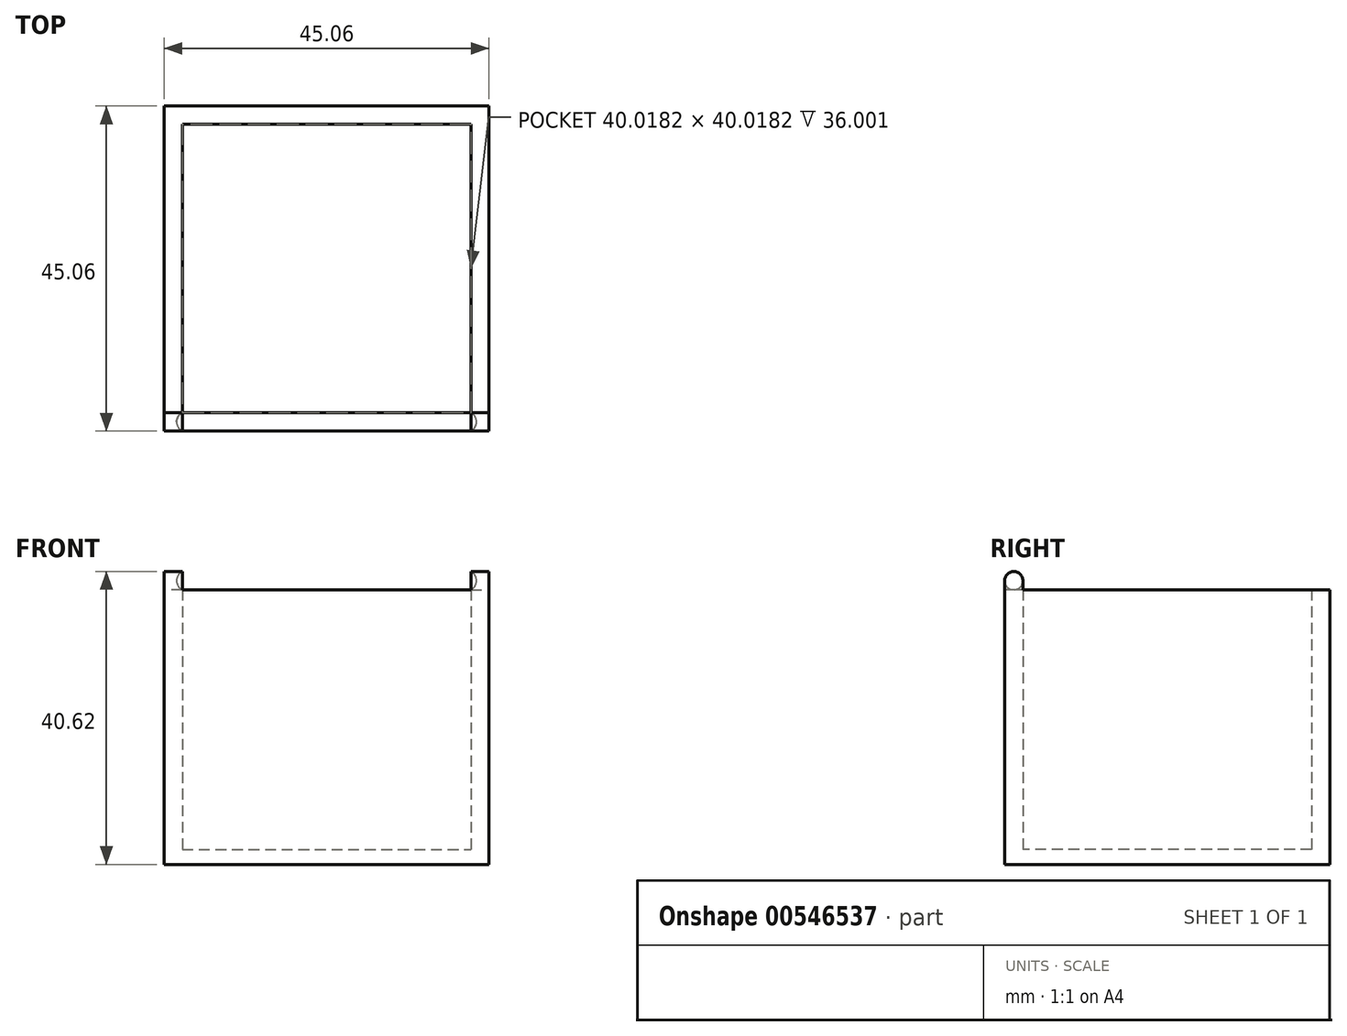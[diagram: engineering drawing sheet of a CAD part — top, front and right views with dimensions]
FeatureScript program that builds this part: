
annotation { "Feature Type Name" : "Feature", "Feature Type Description" : "" }
export const myFeature = defineFeature(function(context is Context, id is Id, definition is map)
    precondition{}
    {
        {
            var Q0;
            Q0=qCreatedBy(makeId("Top.planeOp"),FACE);
            var sketch = newSketch(context, id + "F0", { "sketchPlane" : qUnion([Q0])});
            skCircle(sketch, "E0.cCircle", {"center": v(0, 0) * mm, "radius": 22.53 * mm, "construction": true});
            skLineSegment(sketch, "E0.0", {"start": v(-22.53, -22.53) * mm, "end": v(-22.53, 22.53) * mm});
            skLineSegment(sketch, "E0.1", {"start": v(-22.53, 22.53) * mm, "end": v(22.53, 22.53) * mm});
            skLineSegment(sketch, "E0.2", {"start": v(22.53, 22.53) * mm, "end": v(22.53, -22.53) * mm});
            skLineSegment(sketch, "E0.3", {"start": v(22.53, -22.53) * mm, "end": v(-22.53, -22.53) * mm});
            skPoint(sketch, "E0.0.midPoint", {"position": v(-22.53, 0) * mm});
            skCircle(sketch, "E1.cCircle", {"center": v(0, 0) * mm, "radius": 20 * mm, "construction": true});
            skLineSegment(sketch, "E1.0", {"start": v(-20, -20) * mm, "end": v(-20, 20) * mm});
            skLineSegment(sketch, "E1.1", {"start": v(-20, 20) * mm, "end": v(20, 20) * mm});
            skLineSegment(sketch, "E1.2", {"start": v(20, 20) * mm, "end": v(20, -20) * mm});
            skLineSegment(sketch, "E1.3", {"start": v(20, -20) * mm, "end": v(-20, -20) * mm});
            skPoint(sketch, "E1.0.midPoint", {"position": v(-20, 0) * mm});
            skSolve(sketch);
        }
        {
            var Q0;
            Q0=makeQuery(id+"F0.imprint","IMPRINT",FACE,{"disambiguationData":[TD([[makeQuery(id+"F0.imprint","IMPRINT",EDGE,{"derivedFrom":sQuery(id+"F0.wireOp",EDGE,"E0.0")}),-1.0]])]});
            extrude(context, id + "F1", {"entities" : qUnion([Q0]), "depth" : 38.1 * mm, "offsetDistance" : 25.4 * mm});
        }
        {
            var Q0;
            Q0=makeQuery(id+"F1.opExtrude","CAP_FACE",FACE,{"disambiguationData":[OSD([sQuery(id+"F0.wireOp",EDGE,"E0.0"),sQuery(id+"F0.wireOp",EDGE,"E0.1"),sQuery(id+"F0.wireOp",EDGE,"E0.2"),sQuery(id+"F0.wireOp",EDGE,"E0.3"),sQuery(id+"F0.wireOp",EDGE,"E1.0"),sQuery(id+"F0.wireOp",EDGE,"E1.1"),sQuery(id+"F0.wireOp",EDGE,"E1.2"),sQuery(id+"F0.wireOp",EDGE,"E1.3")])],"isStart":false});
            var sketch = newSketch(context, id + "F2", { "sketchPlane" : qUnion([Q0])});
            skLineSegment(sketch, "E2.bottom", {"start": v(-20, -20) * mm, "end": v(-22.53, -20) * mm});
            skLineSegment(sketch, "E2.top", {"start": v(-20, -22.53) * mm, "end": v(-22.53, -22.53) * mm});
            skLineSegment(sketch, "E2.right", {"start": v(-22.53, -20) * mm, "end": v(-22.53, -22.53) * mm});
            skLineSegment(sketch, "E3.MirrorCS", {"start": v(20, -20) * mm, "end": v(22.53, -20) * mm});
            skLineSegment(sketch, "E4.MirrorCS", {"start": v(22.53, -20) * mm, "end": v(22.53, -22.53) * mm});
            skLineSegment(sketch, "E5.MirrorCS", {"start": v(20, -22.53) * mm, "end": v(22.53, -22.53) * mm});
            skLineSegment(sketch, "E6", {"start": v(-20, -20) * mm, "end": v(-20, -22.53) * mm});
            skLineSegment(sketch, "E7", {"start": v(20, -20) * mm, "end": v(20, -22.53) * mm});
            skSolve(sketch);
        }
        {
            var Q0;
            Q0 = qSketchRegion(id + "F2", true);
            extrude(context, id + "F3", {"entities" : qUnion([Q0]), "operationType" : NewBodyOperationType.ADD, "depth" : 1.26 * mm, "offsetDistance" : 25.4 * mm});
        }
        {
            var Q0;
            Q0=makeQuery(id+"F3.opExtrude","CAP_FACE",FACE,{"disambiguationData":[OSD([sQuery(id+"F2.wireOp",EDGE,"E2.bottom"),sQuery(id+"F2.wireOp",EDGE,"E2.top"),sQuery(id+"F2.wireOp",EDGE,"E2.right"),sQuery(id+"F2.wireOp",EDGE,"E6")])],"isStart":false});
            var sketch = newSketch(context, id + "F4", { "sketchPlane" : qUnion([Q0])});
            skPoint(sketch, "E8", {"position": v(-20, -21.27) * mm});
            skArc(sketch, "E9", {"start": v(-20, -20) * mm, "mid": v(-20.79, -21.27) * mm, "end": v(-20, -22.53) * mm});
            skLineSegment(sketch, "E10", {"start": v(-20, -21.27) * mm, "end": v(-20.79, -21.27) * mm});
            skArc(sketch, "E11.MirrorCS", {"start": v(-20, -22.53) * mm, "mid": v(-20.79, -21.27) * mm, "end": v(-20, -20) * mm});
            skLineSegment(sketch, "E12", {"start": v(-20.79, -21.27) * mm, "end": v(-22.53, -21.27) * mm});
            skPoint(sketch, "E13.MirrorP", {"position": v(20, -21.27) * mm});
            skLineSegment(sketch, "E14.MirrorCS", {"start": v(20, -21.27) * mm, "end": v(20.79, -21.27) * mm});
            skLineSegment(sketch, "E15.MirrorCS", {"start": v(20.79, -21.27) * mm, "end": v(22.53, -21.27) * mm});
            skArc(sketch, "E16.MirrorCS", {"start": v(20, -20) * mm, "mid": v(20.79, -21.27) * mm, "end": v(20, -22.53) * mm});
            skArc(sketch, "E17.MirrorCS", {"start": v(20, -22.53) * mm, "mid": v(20.79, -21.27) * mm, "end": v(20, -20) * mm});
            skLineSegment(sketch, "E18", {"start": v(20, -20) * mm, "end": v(20, -22.53) * mm});
            skLineSegment(sketch, "E19", {"start": v(20, -22.53) * mm, "end": v(22.53, -22.53) * mm});
            skLineSegment(sketch, "E20", {"start": v(22.53, -22.53) * mm, "end": v(22.53, -21.27) * mm});
            skLineSegment(sketch, "E21", {"start": v(22.53, -20) * mm, "end": v(20, -20) * mm});
            skSolve(sketch);
        }
        {
            var Q0;
            {var subQ2=sQuery(id+"F4.wireOp",EDGE,"E12");Q0=makeQuery(id+"F4.imprint","IMPRINT",FACE,{"disambiguationData":[TD([[makeQuery(id+"F4.imprint","IMPRINT",EDGE,{"derivedFrom":subQ2}),-1.0]])]});}
            var Q1;
            {var subQ0=sQuery(id+"F4.wireOp",EDGE,"E15.MirrorCS");Q1=makeQuery(id+"F4.imprint","IMPRINT",FACE,{"disambiguationData":[TD([[makeQuery(id+"F4.imprint","IMPRINT",EDGE,{"derivedFrom":subQ0}),-1.0]])]});}
            var Q2;
            Q2=sQuery(id+"F4.wireOp",EDGE,"E12");
            revolve(context, id + "F5", {"operationType" : NewBodyOperationType.ADD, "entities" : qUnion([Q0, Q1]), "axis" : qUnion([Q2]), "revolveType" : RevolveType.FULL});
        }
        {
            var Q0;
            {var subQ0=sQuery(id+"F4.wireOp",EDGE,"E10");Q0=makeQuery(id+"F4.imprint","IMPRINT",FACE,{"disambiguationData":[TD([[makeQuery(id+"F4.imprint","IMPRINT",EDGE,{"derivedFrom":subQ0}),1.0]])]});}
            var Q1;
            {var subQ0=sQuery(id+"F4.wireOp",EDGE,"E14.MirrorCS");Q1=makeQuery(id+"F4.imprint","IMPRINT",FACE,{"disambiguationData":[TD([[makeQuery(id+"F4.imprint","IMPRINT",EDGE,{"derivedFrom":subQ0}),-1.0]])]});}
            var Q2;
            Q2=sQuery(id+"F4.wireOp",EDGE,"E10");
            revolve(context, id + "F6", {"operationType" : NewBodyOperationType.REMOVE, "entities" : qUnion([Q0, Q1]), "axis" : qUnion([Q2]), "revolveType" : RevolveType.FULL, "oppositeDirection" : true});
        }
        {
            var Q0;
            Q0=makeQuery(id+"F1.opExtrude","SWEPT_FACE",FACE,{"disambiguationData":[OSD([sQuery(id+"F0.wireOp",EDGE,"E1.3")])]});
            var sketch = newSketch(context, id + "F7", { "sketchPlane" : qUnion([Q0])});
            skLineSegment(sketch, "E22.bottom", {"start": v(20, 0) * mm, "end": v(-20, 0) * mm});
            skLineSegment(sketch, "E22.top", {"start": v(20, 2.1) * mm, "end": v(-20, 2.1) * mm});
            skLineSegment(sketch, "E22.left", {"start": v(20, 0) * mm, "end": v(20, 2.1) * mm});
            skLineSegment(sketch, "E22.right", {"start": v(-20, 0) * mm, "end": v(-20, 2.1) * mm});
            skSolve(sketch);
        }
        {
            var Q0;
            Q0 = qSketchRegion(id + "F7", true);
            extrude(context, id + "F8", {"entities" : qUnion([Q0]), "operationType" : NewBodyOperationType.ADD, "depth" : 41.66 * mm, "offsetDistance" : 25.4 * mm});
        }
    });
